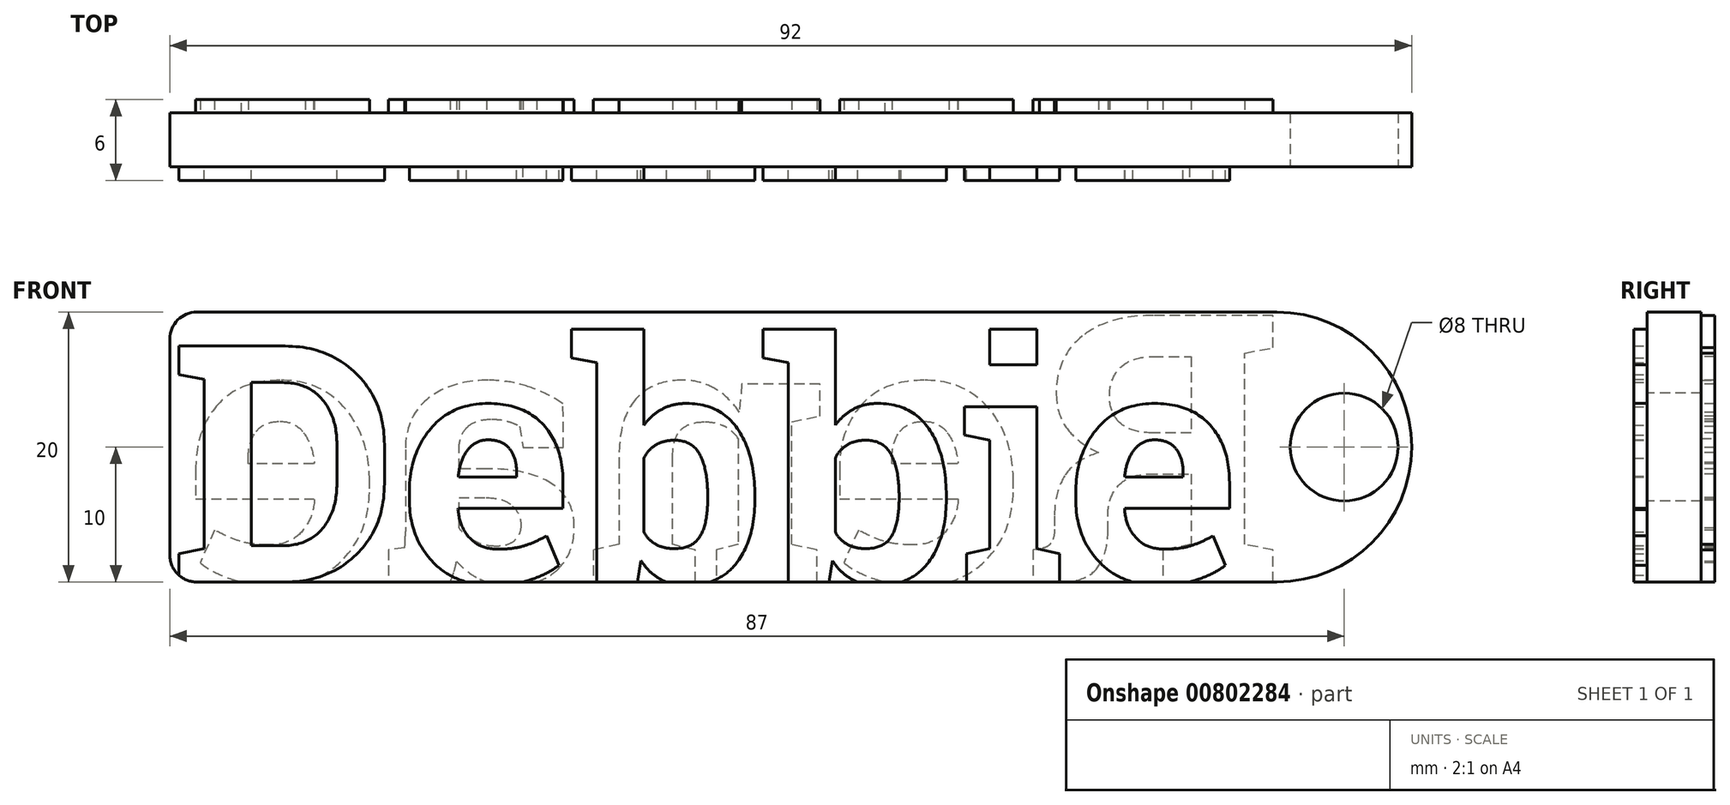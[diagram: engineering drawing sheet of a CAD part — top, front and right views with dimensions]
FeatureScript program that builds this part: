
annotation { "Feature Type Name" : "Feature", "Feature Type Description" : "" }
export const myFeature = defineFeature(function(context is Context, id is Id, definition is map)
    precondition{}
    {
        {
            var Q0;
            Q0=qCreatedBy(makeId("Front.planeOp"),FACE);
            var sketch = newSketch(context, id + "F0", { "sketchPlane" : qUnion([Q0])});
            skText(sketch, "E0", { "text": "Debbie", "fontName": "RobotoSlab-Bold.ttf"});
            const initialGuessF0  = {"E0": [0, 0, 1, 0, 0.0177]};
            skSetInitialGuess(sketch, initialGuessF0);
            skSolve(sketch);
        }
        {
            var Q0;
            Q0 = qSketchRegion(id + "F0", true);
            extrude(context, id + "F1", {"entities" : qUnion([Q0]), "depth" : 1 * mm, "offsetDistance" : 25 * mm});
        }
        {
            var Q0;
            Q0=qCreatedBy(makeId("Front.planeOp"),FACE);
            var sketch = newSketch(context, id + "F2", { "sketchPlane" : qUnion([Q0])});
            skLineSegment(sketch, "E1.bottom", {"start": v(0, 0) * mm, "end": v(82, 0) * mm});
            skLineSegment(sketch, "E1.top", {"start": v(0, 20) * mm, "end": v(82, 20) * mm});
            skLineSegment(sketch, "E1.left", {"start": v(0, 0) * mm, "end": v(0, 20) * mm});
            skLineSegment(sketch, "E1.right", {"start": v(82, 0) * mm, "end": v(82, 20) * mm});
            skSolve(sketch);
        }
        {
            var Q0;
            Q0 = qSketchRegion(id + "F2", true);
            extrude(context, id + "F3", {"entities" : qUnion([Q0]), "operationType" : NewBodyOperationType.ADD, "oppositeDirection" : true, "depth" : 4 * mm, "offsetDistance" : 25 * mm});
        }
        {
            var Q0;
            Q0=makeQuery(id+"F3.opExtrude","CAP_FACE",FACE,{"disambiguationData":[OSD([sQuery(id+"F2.wireOp",EDGE,"E1.bottom"),sQuery(id+"F2.wireOp",EDGE,"E1.top"),sQuery(id+"F2.wireOp",EDGE,"E1.left"),sQuery(id+"F2.wireOp",EDGE,"E1.right")])],"isStart":false});
            var sketch = newSketch(context, id + "F4", { "sketchPlane" : qUnion([Q0])});
            skText(sketch, "E2", { "text": "Renae", "fontName": "RobotoSlab-Bold.ttf"});
            const initialGuessF4  = {"E2": [-0.08249, 0, 1, 0, 0.02]};
            skSetInitialGuess(sketch, initialGuessF4);
            skSolve(sketch);
        }
        {
            var Q0;
            Q0 = qSketchRegion(id + "F4", true);
            extrude(context, id + "F5", {"entities" : qUnion([Q0]), "operationType" : NewBodyOperationType.ADD, "depth" : 1 * mm, "offsetDistance" : 25 * mm});
        }
        {
            var Q0;
            Q0=makeQuery(id+"F3.opExtrude","SWEPT_FACE",FACE,{"disambiguationData":[OSD([sQuery(id+"F2.wireOp",EDGE,"E1.right")])]});
            extrude(context, id + "F6", {"entities" : qUnion([Q0]), "operationType" : NewBodyOperationType.ADD, "depth" : 10 * mm, "offsetDistance" : 25 * mm});
        }
        {
            var Q0;
            Q0=makeQuery(id+"F6.opExtrude","CAP_EDGE",EDGE,{"disambiguationData":[OSD([sQuery(id+"F2.wireOp",EDGE,"E1.top"),sQuery(id+"F2.wireOp",EDGE,"E1.right")])],"isStart":false});
            var Q1;
            Q1=makeQuery(id+"F6.opExtrude","CAP_EDGE",EDGE,{"disambiguationData":[OSD([sQuery(id+"F2.wireOp",EDGE,"E1.bottom"),sQuery(id+"F2.wireOp",EDGE,"E1.right")])],"isStart":false});
            fillet(context, id + "F7", {"entities" : qUnion([Q0, Q1]), "radius" : 10 * mm, "tangentPropagation" : true, "allowEdgeOverflow" : false});
        }
        {
            var Q0;
            {var subQ0=sQuery(id+"F2.wireOp",EDGE,"E1.right");var subQ61=sQuery(id+"F2.wireOp",EDGE,"E1.left");var subQ62=sQuery(id+"F2.wireOp",EDGE,"E1.bottom");var subQ63=sQuery(id+"F2.wireOp",EDGE,"E1.top");Q0=makeQuery(id+"F6.boolean.opBoolean","MERGE",FACE,{"derivedFrom":[makeQuery(id+"F3.boolean.opBoolean","SPLIT",FACE,{"disambiguationData":[TD([makeQuery(id+"F1.opExtrude","SWEPT_FACE",FACE,{"disambiguationData":[OSD([sQuery(id+"F0.wireOp",EDGE,"E0.sketch_text.stroke-0")])]})])],"derivedFrom":makeQuery(id+"F3.opExtrude","CAP_FACE",FACE,{"disambiguationData":[OSD([subQ62,subQ63,subQ61,subQ0])],"isStart":true})}),makeQuery(id+"F6.opExtrude","SWEPT_FACE",FACE,{"disambiguationData":[OSD([subQ0]),TDD([makeQuery(id+"F3.opExtrude","CAP_EDGE",EDGE,{"disambiguationData":[OSD([subQ0])],"isStart":true})])]})]});}
            var sketch = newSketch(context, id + "F8", { "sketchPlane" : qUnion([Q0])});
            skCircle(sketch, "E3", {"center": v(87, 10) * mm, "radius": 4 * mm});
            skPoint(sketch, "E3.centerSnap0", {"position": v(92, 10) * mm});
            skLineSegment(sketch, "E4", {"start": v(87, 10) * mm, "end": v(92, 10) * mm});
            skSolve(sketch);
        }
        {
            var Q0;
            Q0=makeQuery(id+"F8.imprint","IMPRINT",FACE,{"disambiguationData":[TD([[makeQuery(id+"F8.imprint","IMPRINT",EDGE,{"derivedFrom":sQuery(id+"F8.wireOp",EDGE,"E3")}),1.0]])]});
            extrude(context, id + "F9", {"entities" : qUnion([Q0]), "operationType" : NewBodyOperationType.REMOVE, "oppositeDirection" : true, "depth" : 25 * mm, "offsetDistance" : 25 * mm});
        }
        {
            var Q0;
            Q0=makeQuery(id+"F3.opExtrude","SWEPT_EDGE",EDGE,{"disambiguationData":[OSD([sQuery(id+"F2.wireOp",EDGE,"E1.top"),sQuery(id+"F2.wireOp",EDGE,"E1.left")])]});
            var Q1;
            Q1=makeQuery(id+"F3.opExtrude","SWEPT_EDGE",EDGE,{"disambiguationData":[OSD([sQuery(id+"F2.wireOp",EDGE,"E1.bottom"),sQuery(id+"F2.wireOp",EDGE,"E1.left")])]});
            fillet(context, id + "F10", {"entities" : qUnion([Q0, Q1]), "radius" : 2 * mm, "tangentPropagation" : true, "allowEdgeOverflow" : false});
        }
        {
            var Q0;
            Q0=makeQuery(id+"F3.opExtrude","SWEPT_FACE",FACE,{"disambiguationData":[OSD([sQuery(id+"F2.wireOp",EDGE,"E1.left")])]});
            var sketch = newSketch(context, id + "F11", { "sketchPlane" : qUnion([Q0])});
            skLineSegment(sketch, "E5", {"start": v(-2, 2) * mm, "end": v(-2, 0) * mm});
            skLineSegment(sketch, "E6", {"start": v(-2, 0) * mm, "end": v(-6.24, 0) * mm});
            skLineSegment(sketch, "E7", {"start": v(-6.24, 0) * mm, "end": v(-6.24, -1.2) * mm});
            skLineSegment(sketch, "E8", {"start": v(-6.24, -1.2) * mm, "end": v(2.95, -1.2) * mm});
            skLineSegment(sketch, "E9", {"start": v(2.95, -1.2) * mm, "end": v(2.95, 0) * mm});
            skLineSegment(sketch, "E10", {"start": v(2.95, 0) * mm, "end": v(-2, 0) * mm});
            skSolve(sketch);
        }
        {
            var Q0;
            Q0 = qSketchRegion(id + "F11", true);
            extrude(context, id + "F12", {"entities" : qUnion([Q0]), "operationType" : NewBodyOperationType.REMOVE, "oppositeDirection" : true, "depth" : 94.3 * mm, "offsetDistance" : 25 * mm});
        }
    });
